# Revit family: Sense allas
name_source: partatom
category: Casework
revit_build: Autodesk Revit 2015 (Build: 20140606_1530(x64)
units: mm (PartAtom-declared; Revit-internal decimal feet)

## types (6) — shared parameters
Basin color = Cast Marble - White
Drain Pipe Material = Chrome - Polished
Handrail Color = RAL 9016 - White
Height = 800 mm  [stored 2.62467 ft]
Keynote = 62022
Manufacturer = Väinö Korpinen Oy
Model = Sense allas
URL = www.korpinen.com
Width = 900 mm

## per-type parameters (varying)
| type | Accent | Accent colour | Left | Right |
| 62022WAM | No | Red | No | Yes |
| 62022GAM | Yes | Grey | No | Yes |
| 62022RAM | Yes | Red | No | Yes |
| 62023WAM | No | Red | Yes | No |
| 62023RAM | Yes | Red | Yes | No |
| 62023GAM | Yes | Grey | Yes | No |

note: [stored X ft] marks values corroborated as IEEE doubles in the binary element streams (Revit-internal decimal feet)

## geometry (parser evidence)
native form markers: Blend x4, Sweep x14
no freeform markers — native parametric forms only
